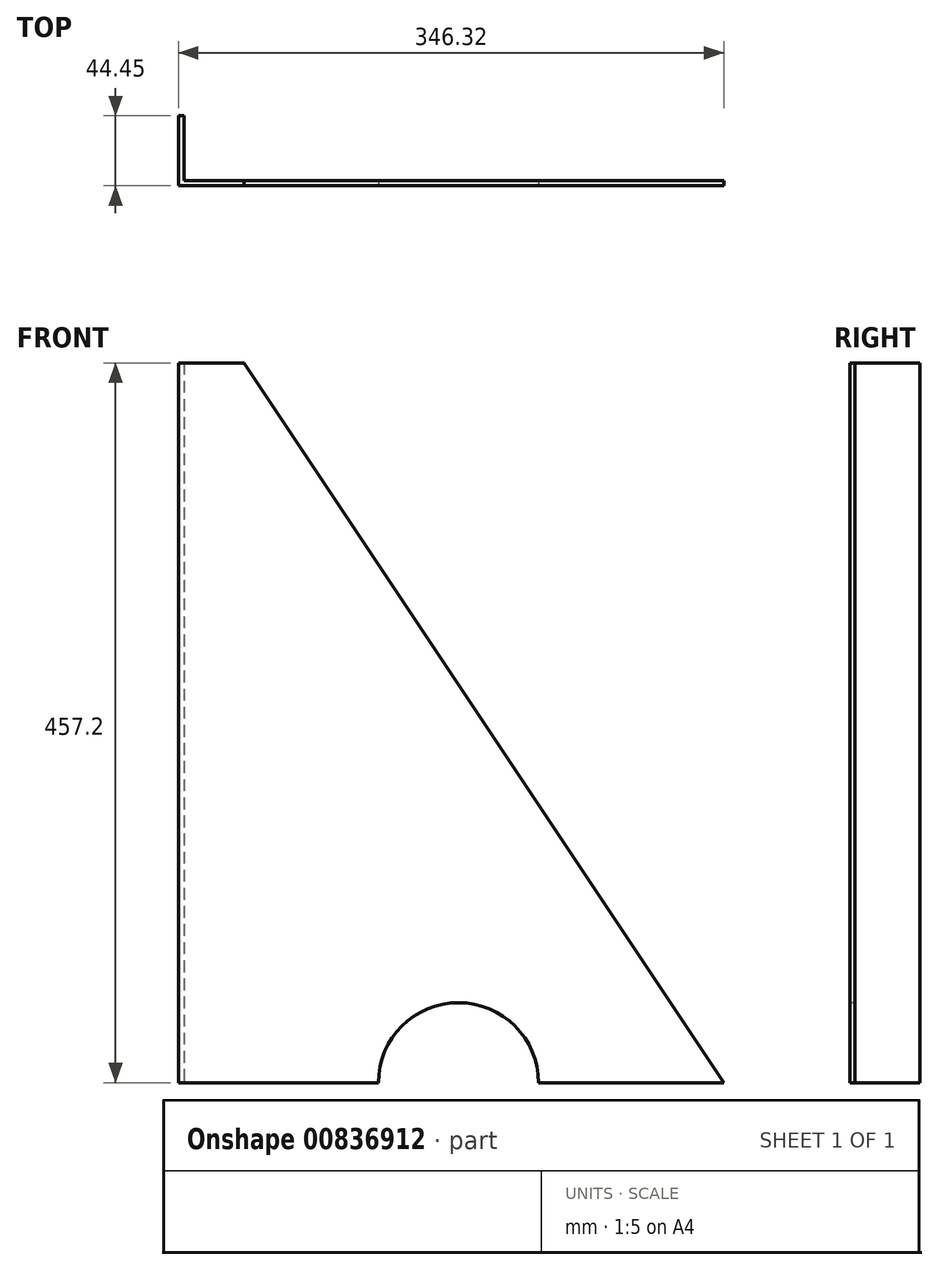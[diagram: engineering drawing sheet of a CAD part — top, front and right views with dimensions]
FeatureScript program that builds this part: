
annotation { "Feature Type Name" : "Feature", "Feature Type Description" : "" }
export const myFeature = defineFeature(function(context is Context, id is Id, definition is map)
    precondition{}
    {
        {
            var Q0;
            Q0=qCreatedBy(makeId("Front.planeOp"),FACE);
            var sketch = newSketch(context, id + "F0", { "sketchPlane" : qUnion([Q0])});
            skLineSegment(sketch, "E0", {"start": v(0, 0) * mm, "end": v(304.8, 0) * mm});
            skLineSegment(sketch, "E1", {"start": v(304.8, 0) * mm, "end": v(0, 457.2) * mm});
            skLineSegment(sketch, "E2", {"start": v(0, 457.2) * mm, "end": v(0, 0) * mm});
            skSolve(sketch);
        }
        {
            var Q0;
            Q0 = qSketchRegion(id + "F0", true);
            extrude(context, id + "F1", {"entities" : qUnion([Q0]), "depth" : 3.42 * mm, "offsetDistance" : 25.4 * mm});
        }
        {
            var Q0;
            Q0=qCreatedBy(makeId("Top.planeOp"),FACE);
            var sketch = newSketch(context, id + "F2", { "sketchPlane" : qUnion([Q0])});
            skLineSegment(sketch, "E3.bottom", {"start": v(0, 0) * mm, "end": v(-38.1, 0) * mm});
            skLineSegment(sketch, "E3.right", {"start": v(-38.1, 0) * mm, "end": v(-38.1, 41.03) * mm});
            skLineSegment(sketch, "E4.bottom", {"start": v(0, -3.42) * mm, "end": v(-41.52, -3.42) * mm});
            skLineSegment(sketch, "E4.left", {"start": v(0, -3.42) * mm, "end": v(0, 0) * mm});
            skLineSegment(sketch, "E4.right", {"start": v(-41.52, -3.42) * mm, "end": v(-41.52, 41.03) * mm});
            skLineSegment(sketch, "E5", {"start": v(-38.1, 41.03) * mm, "end": v(-41.52, 41.03) * mm});
            skSolve(sketch);
        }
        {
            var Q0;
            Q0 = qSketchRegion(id + "F2", true);
            var Q1;
            Q1=makeQuery(id+"F1.opExtrude","CAP_VERTEX",VERTEX,{"disambiguationData":[OSD([sQuery(id+"F0.wireOp",EDGE,"E1"),sQuery(id+"F0.wireOp",EDGE,"E2")])],"isStart":false});
            extrude(context, id + "F3", {"entities" : qUnion([Q0]), "operationType" : NewBodyOperationType.ADD, "endBound" : BoundingType.UP_TO_VERTEX, "depth" : 406.4 * mm, "endBoundEntityVertex" : qUnion([Q1]), "offsetDistance" : 25.4 * mm});
        }
        {
            var Q0;
            Q0=makeQuery(id+"F3.boolean.opBoolean","MERGE",FACE,{"derivedFrom":[makeQuery(id+"F1.opExtrude","CAP_FACE",FACE,{"disambiguationData":[OSD([sQuery(id+"F0.wireOp",EDGE,"E0"),sQuery(id+"F0.wireOp",EDGE,"E1"),sQuery(id+"F0.wireOp",EDGE,"E2")])],"isStart":false}),makeQuery(id+"F3.opExtrude","SWEPT_FACE",FACE,{"disambiguationData":[OSD([sQuery(id+"F2.wireOp",EDGE,"E4.bottom")])]})]});
            var sketch = newSketch(context, id + "F4", { "sketchPlane" : qUnion([Q0])});
            skCircle(sketch, "E6", {"center": v(136.28, 0) * mm, "radius": 50.8 * mm});
            skSolve(sketch);
        }
        {
            var Q0;
            Q0 = qSketchRegion(id + "F4", true);
            extrude(context, id + "F5", {"entities" : qUnion([Q0]), "operationType" : NewBodyOperationType.REMOVE, "oppositeDirection" : true, "depth" : 25.4 * mm, "offsetDistance" : 25.4 * mm});
        }
    });
